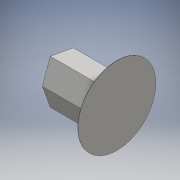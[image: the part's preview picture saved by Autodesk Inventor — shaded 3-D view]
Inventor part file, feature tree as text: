
AUTODESK INVENTOR PART (.ipt)
format: ipt  version: 2016 (Build 200138000, 138)  size: 116,224 bytes
history: native  units: mm
features: other x3, extrude x2, sketch x2, fillet x1
ambient origin geometry x8: Origin, YZ Plane, XZ Plane, XY Plane, X Axis, Y Axis, Z Axis, Center Point
bodies: Solid1 (feature_tree)
feature tree (8):
  other  "Blocks"
  extrude  "Extrusion1"  Depth=21.0mm TaperAngle=0.0deg
  extrude  "Extrusion2"  Depth=2.0mm
  fillet  "Fillet1"  [1 undecoded]
  sketch  "Sketch1"  dims[d3=2.9mm d4=21.0mm d5=0.0mm]
  other  "Block1"
  sketch  "Sketch2"  dims[d6=0.1mm d7=0.0mm d8=2.0mm]
  other  "Block1:1"
note: 1 required parameter value undecoded (feature->parameter linkage not recoverable at this tier; creation-order binding heuristic only, values carry confidence <= 0.55)
